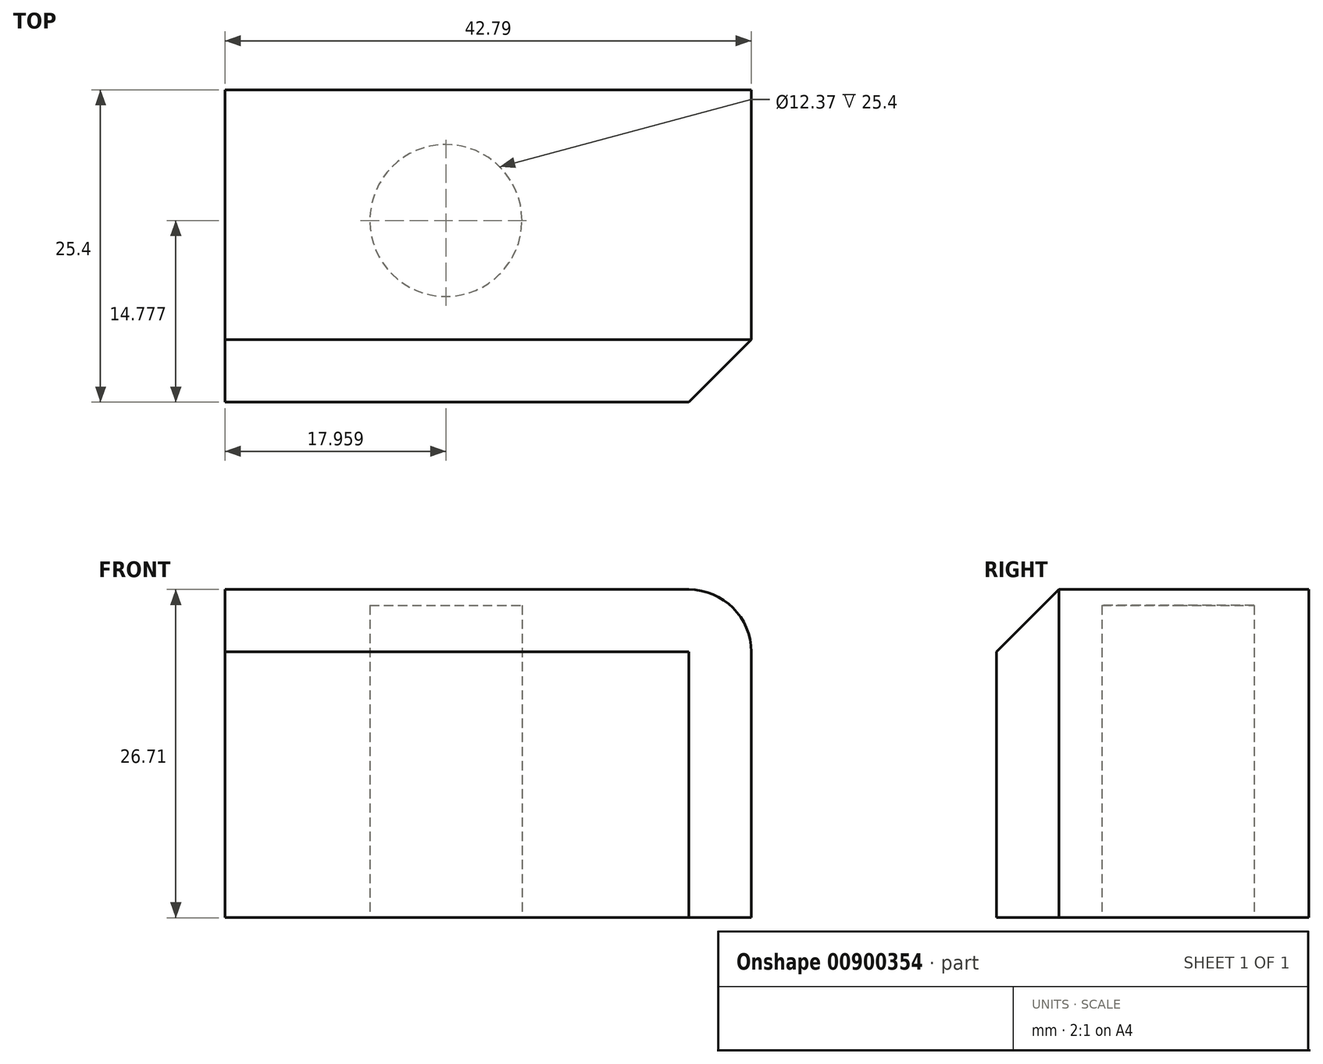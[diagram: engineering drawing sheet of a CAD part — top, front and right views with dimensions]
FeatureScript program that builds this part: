
annotation { "Feature Type Name" : "Feature", "Feature Type Description" : "" }
export const myFeature = defineFeature(function(context is Context, id is Id, definition is map)
    precondition{}
    {
        {
            var Q0;
            Q0=qCreatedBy(makeId("Front.planeOp"),FACE);
            var sketch = newSketch(context, id + "F0", { "sketchPlane" : qUnion([Q0])});
            skLineSegment(sketch, "E0.bottom", {"start": v(-134.72, 3.6) * mm, "end": v(-91.93, 3.6) * mm});
            skLineSegment(sketch, "E0.top", {"start": v(-134.72, 30.3) * mm, "end": v(-91.93, 30.3) * mm});
            skLineSegment(sketch, "E0.left", {"start": v(-134.72, 3.6) * mm, "end": v(-134.72, 30.3) * mm});
            skLineSegment(sketch, "E0.right", {"start": v(-91.93, 3.6) * mm, "end": v(-91.93, 30.3) * mm});
            skSolve(sketch);
        }
        {
            var Q0;
            Q0 = qSketchRegion(id + "F0", true);
            extrude(context, id + "F1", {"entities" : qUnion([Q0]), "depth" : 25.4 * mm, "offsetDistance" : 25.4 * mm});
        }
        {
            var Q0;
            Q0=makeQuery(id+"F1.opExtrude","SWEPT_EDGE",EDGE,{"disambiguationData":[OSD([sQuery(id+"F0.wireOp",EDGE,"E0.top"),sQuery(id+"F0.wireOp",EDGE,"E0.right")])]});
            fillet(context, id + "F2", {"entities" : qUnion([Q0]), "radius" : 5.08 * mm, "tangentPropagation" : true, "allowEdgeOverflow" : false});
        }
        {
            var Q0;
            Q0=makeQuery(id+"F1.opExtrude","CAP_EDGE",EDGE,{"disambiguationData":[OSD([sQuery(id+"F0.wireOp",EDGE,"E0.top")])],"isStart":false});
            chamfer(context, id + "F3", {"entities" : qUnion([Q0]), "width" : 5.08 * mm, "tangentPropagation" : true});
        }
        {
            var Q0;
            Q0=makeQuery(id+"F1.opExtrude","SWEPT_FACE",FACE,{"disambiguationData":[OSD([sQuery(id+"F0.wireOp",EDGE,"E0.bottom")])]});
            var sketch = newSketch(context, id + "F4", { "sketchPlane" : qUnion([Q0])});
            skCircle(sketch, "E1", {"center": v(-116.76, 10.62) * mm, "radius": 6.18 * mm});
            skSolve(sketch);
        }
        {
            var Q0;
            Q0 = qSketchRegion(id + "F4", true);
            extrude(context, id + "F5", {"entities" : qUnion([Q0]), "operationType" : NewBodyOperationType.REMOVE, "oppositeDirection" : true, "depth" : 25.4 * mm, "offsetDistance" : 25.4 * mm});
        }
    });
